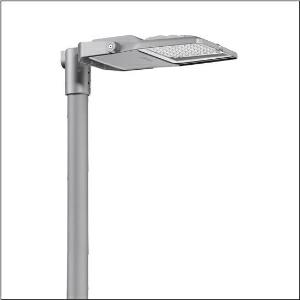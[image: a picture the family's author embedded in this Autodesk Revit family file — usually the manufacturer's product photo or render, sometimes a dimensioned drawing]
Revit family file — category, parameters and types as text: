
# Revit family: floodlight_fl_21_iq_mini___pl43_5xa7772d4a3a_0702
name_source: partatom
category: Lighting Fixtures
units: mm (PartAtom-declared; Revit-internal decimal feet)

## family parameters
Cut with Voids When Loaded = No
Host = Face
Light Source = No
Part Type = Normal
Room Calculation Point = No
Round Connector Dimension = Use Diameter
Shared = No

## types (1)
- --- (1 x LED, 19090 lm, 143 W, 4000K)
    Apparent Load = 143 VA
    CIE Flux Codes = 27 78 99 100 100
    Color Rendering = 70
    Color Temperature = 4000K
    Default Elevation = 1800 mm
    Description = Floodlight FL 21 iQ mini, floodlight, primary light control with lens, of PMMA, primary optical cover: protective disc, of toughened safety glass, transparent, light distribution: PL43, light emission: direct distribution, installation type: surface-mounted, LED, High Power LED, rated luminous flux: 19.090lm, luminous efficacy: 134lm/W, light colour: 740, colour temperature: 4000K, control: Auto-Match, Temp-Guard, Night-Set, Smart-Wire, Desk-Remote (wireless, voltage-free reading and setting of iQ features in the workshop via application-optimized NFC function/RFID function), optimised constant luminous flux control (CLO 2.0), Light-Fading, Lumen-Switch, with terminal, 6-pole, mains connection: 220..240V, AC, 50/60Hz, start of lifetime: 143W, end of service life: 152W, reduction: 61W, luminaire housing, of diecast aluminium, powder-coated, Siteco® metallic grey (DB 702S), corrosivity category C5 mid according to DIN EN ISO 12944, sealing non-destructively replaceable, please order mast flange separately, mast bracket, of steel, galvanised, powder-coated, protection rating (complete): IP66, insulation class (complete): insulation class II (safety insulation), certification: CE, ENEC, VDE, protection symbol: D, impact resistance: IK08, permissible operating ambient temperature: -40..+40°C, permissible operating ambient temperature for outdoor applications: -40..+50°C, standard: DIN EN 12944, LABS conformity tested according to VDMA 24364:2018-05, packaging unit: 1 piece

Light Distribution: PL43
    Height = 70 mm
    Lamp = 1 x LED
    Lamp Light Flux = 19090 lm
    Lamp Power = 143 W
    Lamp count = 1
    Length = 485 mm
    Luminous efficacy = 133 lm/W
    Manufacturer = Siteco
    ModVariant = No
    Model = 5XA7772D4A3A
    Number of Poles = 1
    OnlyDefault = Yes
    Power Factor = 1
    Product Name = Floodlight FL 21 iQ mini | PL43
    Product group = floodlight | pylon annexe
    ProductGroupID = 6200
    Protection Class = Protection class II
    Protection Degree = IP 66
    RLX_Detail_Level = 1
    RLX_Emergency_Light_Flux = 0 lm
    RLX_Emergency_Type = 0
    RLX_Emergency_Type_DB = No
    RlxData = <blob elided: 101513 chars, md5=cb70dcaa>
    Socket = socket
    Standby Power = 0 W
    System Light Flux = 19090 lm
    System Power = 143 W
    Type Comments = factory setting: luminous flux: 100 % | dim-lin: 254 | 730 mA
    Type Image = l_1007125.jpg
    URL = http://relux.com
    VarID = @adj_111625
    Voltage = 0 V
    Weight = 0.00 kg
    Width = 337 mm

## geometry (parser evidence)
native form markers: Blend x4, Sweep x12
no freeform markers — native parametric forms only
